# Revit family: 201_PRO-_-B+NCD
name_source: partatom
category: Air Terminals
units: mm (PartAtom-declared; Revit-internal decimal feet)

## family parameters
Always vertical = Yes
Cut with Voids When Loaded = No
Part Type = Normal
Room Calculation Point = Yes
Round Connector Dimension = Use Diameter
Shared = No
Work Plane-Based = No

## types (5) — shared parameters
CAT0 = Yes
CL_Location_5000 = 5000 mm  [stored 16.4042 ft]
DZ = 5 mm  [stored 0.0164042 ft]
Description = EXPANSION BOXES
L_ARR = 400 mm  [stored 1.31234 ft]
Manufacturer = Alnor
QmdConnectorList = 201;D
SW1 = Yes
SW2 = No
URL = http://www.ventilation-alnor.co.uk
W_ARR = 400 mm  [stored 1.31234 ft]
XRefLineVPlnId = 7453
YRefLineVPlnId = 7456
magiPartTypeId = 201
magiProductFamilyId = PRO-*-B+NCD
zero-valued in all types: CLBTZ, H_ARR

## per-type parameters (varying)
| type | CLD | D | DA | DPZ | PH | PL | PL2 | ZC |
| PRO-150-B+NCD | 225 mm  [stored 0.738189 ft] | 150 mm | 257 mm  [stored 0.843176 ft] | 130 mm | 270 mm  [stored 0.885827 ft] | 280 mm  [stored 0.918635 ft] | 140 mm  [stored 0.459318 ft] | 270 mm  [stored 0.885827 ft] |
| PRO-350-B+NCD | 425 mm | 350 mm | 457 mm | 215 mm | 440 mm | 480 mm | 240 mm | 440 mm |
| PRO-300-B+NCD | 375 mm | 300 mm | 407 mm | 190 mm | 390 mm | 430 mm | 215 mm | 390 mm |
| PRO-250-B+NCD | 325 mm | 250 mm | 357 mm | 170 mm | 350 mm | 385 mm | 193 mm | 350 mm |
| PRO-200-B+NCD | 275 mm | 200 mm | 307 mm | 150 mm  [stored 0.492126 ft] | 310 mm | 330 mm | 165 mm | 310 mm |

note: column(s) folded — value = type name in every type: MC Product Code, magiProductId

note: [stored X ft] marks values corroborated as IEEE doubles in the binary element streams (Revit-internal decimal feet)

## geometry (parser evidence)
native form markers: Blend x2, Sweep x2
no freeform markers — native parametric forms only
